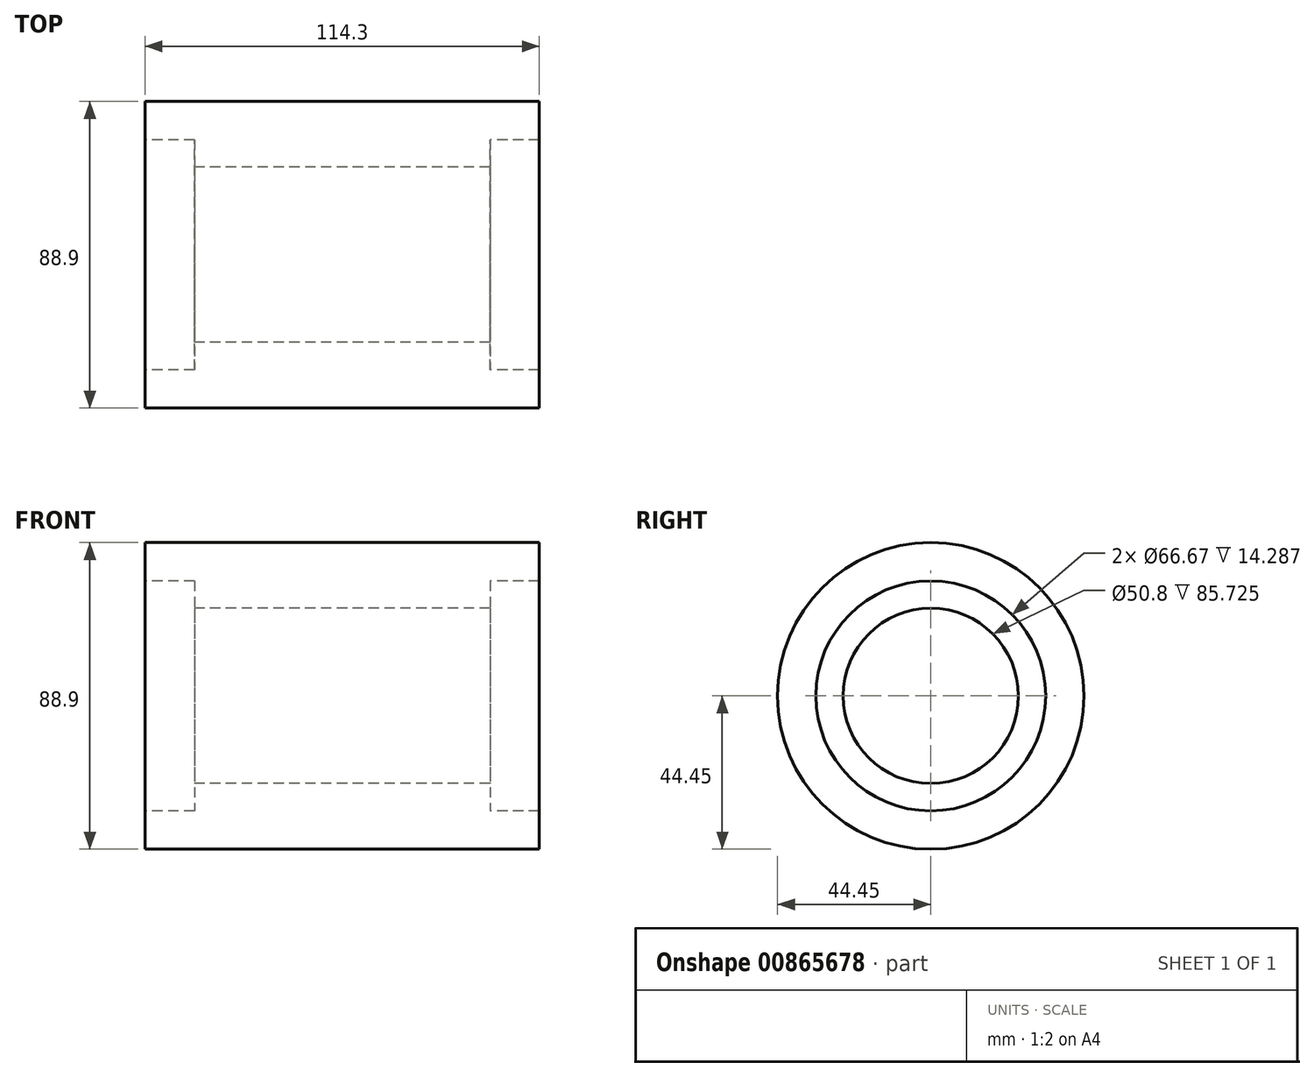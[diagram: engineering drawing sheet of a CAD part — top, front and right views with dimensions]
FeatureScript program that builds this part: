
annotation { "Feature Type Name" : "Feature", "Feature Type Description" : "" }
export const myFeature = defineFeature(function(context is Context, id is Id, definition is map)
    precondition{}
    {
        {
            var Q0;
            Q0=qCreatedBy(makeId("Front.planeOp"),FACE);
            var sketch = newSketch(context, id + "F0", { "sketchPlane" : qUnion([Q0])});
            skLineSegment(sketch, "E0", {"start": v(-64.85, 0) * mm, "end": v(63.16, 0) * mm, "construction": true});
            skLineSegment(sketch, "E1", {"start": v(-67.33, -25.4) * mm, "end": v(18.4, -25.4) * mm});
            skLineSegment(sketch, "E2", {"start": v(18.4, -25.4) * mm, "end": v(18.4, -33.34) * mm});
            skLineSegment(sketch, "E3", {"start": v(18.4, -33.34) * mm, "end": v(32.68, -33.34) * mm});
            skLineSegment(sketch, "E4", {"start": v(32.68, -33.34) * mm, "end": v(32.68, -44.45) * mm});
            skLineSegment(sketch, "E5", {"start": v(32.68, -44.45) * mm, "end": v(-81.62, -44.45) * mm});
            skLineSegment(sketch, "E6", {"start": v(-81.62, -44.45) * mm, "end": v(-81.62, -33.34) * mm});
            skLineSegment(sketch, "E7", {"start": v(-81.62, -33.34) * mm, "end": v(-67.33, -33.34) * mm});
            skLineSegment(sketch, "E8", {"start": v(-67.33, -33.34) * mm, "end": v(-67.33, -25.4) * mm});
            skSolve(sketch);
        }
        {
            var Q0;
            Q0=makeQuery(id+"F0.imprint","IMPRINT",FACE,{"disambiguationData":[TD([[makeQuery(id+"F0.imprint","IMPRINT",EDGE,{"derivedFrom":sQuery(id+"F0.wireOp",EDGE,"E1")}),-1.0]])]});
            var Q1;
            Q1=sQuery(id+"F0.wireOp",EDGE,"E0");
            revolve(context, id + "F1", {"surfaceOperationType" : NewSurfaceOperationType.NEW, "entities" : qUnion([Q0]), "axis" : qUnion([Q1]), "revolveType" : RevolveType.FULL});
        }
    });
